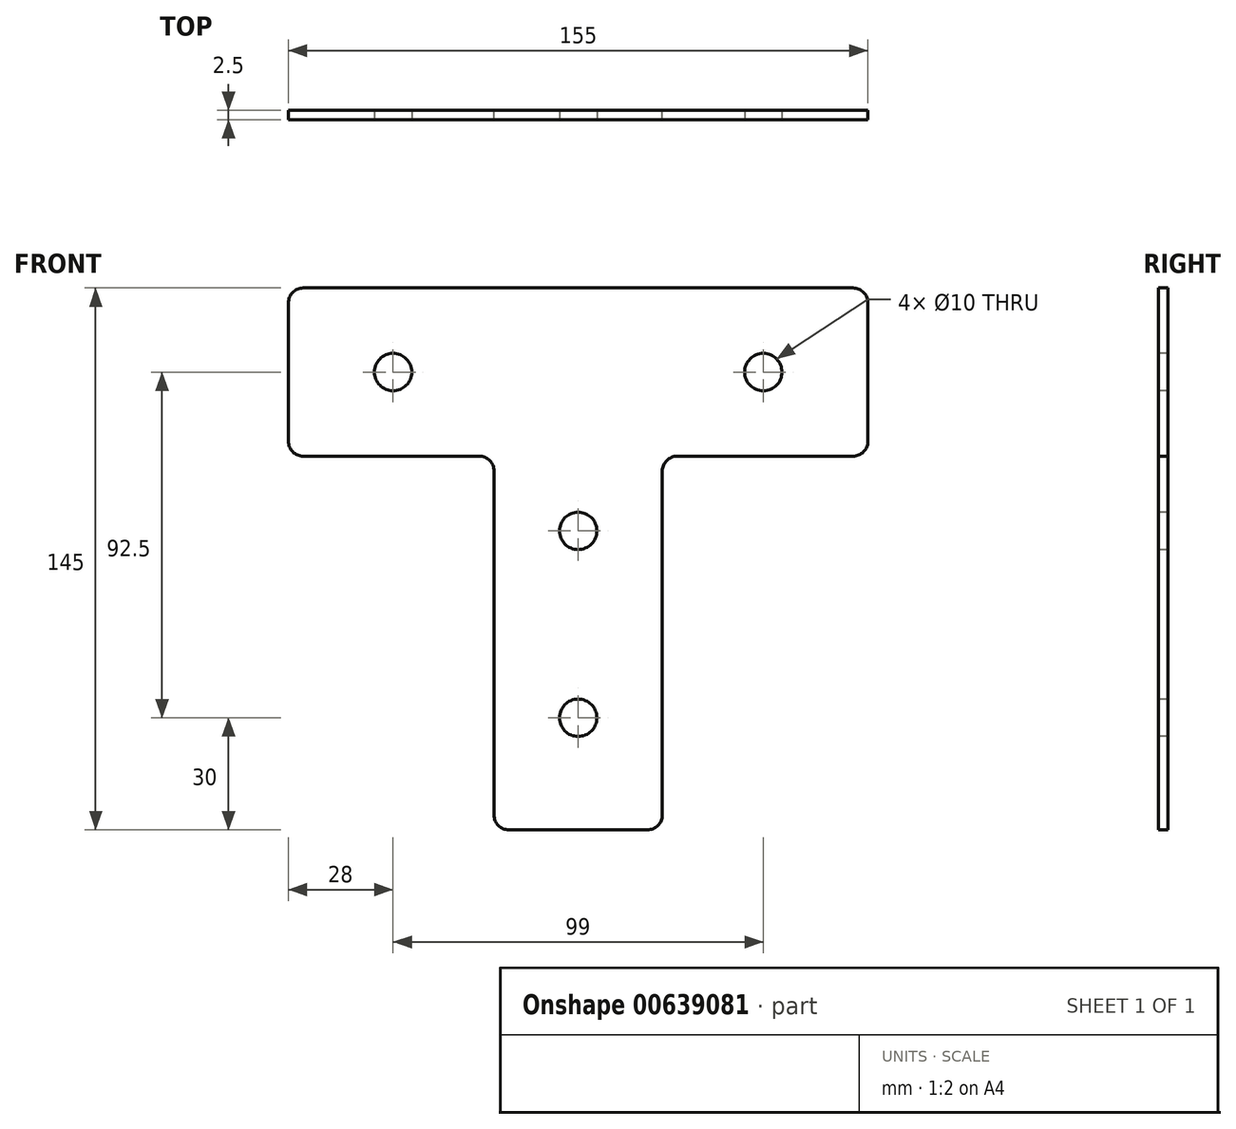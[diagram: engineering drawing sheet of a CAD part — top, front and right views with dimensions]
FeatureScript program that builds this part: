
annotation { "Feature Type Name" : "Feature", "Feature Type Description" : "" }
export const myFeature = defineFeature(function(context is Context, id is Id, definition is map)
    precondition{}
    {
        {
            var Q0;
            Q0=qCreatedBy(makeId("Front.planeOp"),FACE);
            var sketch = newSketch(context, id + "F0", { "sketchPlane" : qUnion([Q0])});
            skLineSegment(sketch, "E0.bottom", {"start": v(-77.5, 22.5) * mm, "end": v(77.5, 22.5) * mm});
            skLineSegment(sketch, "E0.top", {"start": v(-77.5, -22.5) * mm, "end": v(-22.5, -22.5) * mm});
            skLineSegment(sketch, "E0.left", {"start": v(-77.5, 22.5) * mm, "end": v(-77.5, -22.5) * mm});
            skLineSegment(sketch, "E0.right", {"start": v(77.5, 22.5) * mm, "end": v(77.5, -22.5) * mm});
            skPoint(sketch, "E0.middle", {"position": v(0, 0) * mm});
            skLineSegment(sketch, "E1", {"start": v(77.5, -22.5) * mm, "end": v(22.5, -22.5) * mm});
            skLineSegment(sketch, "E2", {"start": v(22.5, -22.5) * mm, "end": v(22.5, -122.5) * mm});
            skLineSegment(sketch, "E3", {"start": v(22.5, -122.5) * mm, "end": v(-22.5, -122.5) * mm});
            skLineSegment(sketch, "E4", {"start": v(-22.5, -122.5) * mm, "end": v(-22.5, -22.5) * mm});
            skLineSegment(sketch, "E5", {"start": v(-22.5, -22.5) * mm, "end": v(-77.5, -22.5) * mm});
            skLineSegment(sketch, "E6.trimOffspring", {"start": v(22.5, -22.5) * mm, "end": v(77.5, -22.5) * mm});
            skSolve(sketch);
        }
        {
            var Q0;
            Q0 = qSketchRegion(id + "F0", true);
            extrude(context, id + "F1", {"entities" : qUnion([Q0]), "depth" : 2.5 * mm, "offsetDistance" : 25 * mm});
        }
        {
            var Q0;
            Q0=makeQuery(id+"F1.opExtrude","SWEPT_EDGE",EDGE,{"disambiguationData":[OSD([sQuery(id+"F0.wireOp",EDGE,"E0.bottom"),sQuery(id+"F0.wireOp",EDGE,"E0.left")])]});
            var Q1;
            Q1=makeQuery(id+"F1.opExtrude","SWEPT_EDGE",EDGE,{"disambiguationData":[OSD([sQuery(id+"F0.wireOp",EDGE,"E0.left"),sQuery(id+"F0.wireOp",EDGE,"E5")])]});
            var Q2;
            Q2=makeQuery(id+"F1.opExtrude","SWEPT_EDGE",EDGE,{"disambiguationData":[OSD([sQuery(id+"F0.wireOp",EDGE,"E0.bottom"),sQuery(id+"F0.wireOp",EDGE,"E0.right")])]});
            var Q3;
            Q3=makeQuery(id+"F1.opExtrude","SWEPT_EDGE",EDGE,{"disambiguationData":[OSD([sQuery(id+"F0.wireOp",EDGE,"E0.right"),sQuery(id+"F0.wireOp",EDGE,"E6.trimOffspring")])]});
            var Q4;
            Q4=makeQuery(id+"F1.opExtrude","SWEPT_EDGE",EDGE,{"disambiguationData":[OSD([sQuery(id+"F0.wireOp",EDGE,"E2"),sQuery(id+"F0.wireOp",EDGE,"E3")])]});
            var Q5;
            Q5=makeQuery(id+"F1.opExtrude","SWEPT_EDGE",EDGE,{"disambiguationData":[OSD([sQuery(id+"F0.wireOp",EDGE,"E3"),sQuery(id+"F0.wireOp",EDGE,"E4")])]});
            var Q6;
            Q6=makeQuery(id+"F1.opExtrude","SWEPT_EDGE",EDGE,{"disambiguationData":[OSD([sQuery(id+"F0.wireOp",EDGE,"E2"),sQuery(id+"F0.wireOp",EDGE,"E6.trimOffspring")])]});
            var Q7;
            Q7=makeQuery(id+"F1.opExtrude","SWEPT_EDGE",EDGE,{"disambiguationData":[OSD([sQuery(id+"F0.wireOp",EDGE,"E4"),sQuery(id+"F0.wireOp",EDGE,"E5")])]});
            fillet(context, id + "F2", {"entities" : qUnion([Q0, Q1, Q2, Q3, Q4, Q5, Q6, Q7]), "radius" : 4 * mm, "tangentPropagation" : true, "allowEdgeOverflow" : false});
        }
        {
            var Q0;
            Q0=makeQuery(id+"F1.opExtrude","CAP_FACE",FACE,{"disambiguationData":[OSD([sQuery(id+"F0.wireOp",EDGE,"E0.bottom"),sQuery(id+"F0.wireOp",EDGE,"E0.left"),sQuery(id+"F0.wireOp",EDGE,"E0.right"),sQuery(id+"F0.wireOp",EDGE,"E2"),sQuery(id+"F0.wireOp",EDGE,"E3"),sQuery(id+"F0.wireOp",EDGE,"E4"),sQuery(id+"F0.wireOp",EDGE,"E5"),sQuery(id+"F0.wireOp",EDGE,"E6.trimOffspring")])],"isStart":false});
            var sketch = newSketch(context, id + "F3", { "sketchPlane" : qUnion([Q0])});
            skCircle(sketch, "E7", {"center": v(-49.5, 0) * mm, "radius": 5 * mm});
            skCircle(sketch, "E8", {"center": v(49.5, 0) * mm, "radius": 5 * mm});
            skCircle(sketch, "E9", {"center": v(0, -92.5) * mm, "radius": 5 * mm});
            skSolve(sketch);
        }
        {
            var Q0;
            Q0=makeQuery(id+"F3.imprint","IMPRINT",FACE,{"disambiguationData":[TD([[makeQuery(id+"F3.imprint","IMPRINT",EDGE,{"derivedFrom":sQuery(id+"F3.wireOp",EDGE,"E8")}),1.0]])]});
            var Q1;
            Q1=makeQuery(id+"F3.imprint","IMPRINT",FACE,{"disambiguationData":[TD([[makeQuery(id+"F3.imprint","IMPRINT",EDGE,{"derivedFrom":sQuery(id+"F3.wireOp",EDGE,"E7")}),1.0]])]});
            var Q2;
            Q2=makeQuery(id+"F3.imprint","IMPRINT",FACE,{"disambiguationData":[TD([[makeQuery(id+"F3.imprint","IMPRINT",EDGE,{"derivedFrom":sQuery(id+"F3.wireOp",EDGE,"E9")}),1.0]])]});
            extrude(context, id + "F4", {"entities" : qUnion([Q0, Q1, Q2]), "operationType" : NewBodyOperationType.REMOVE, "endBound" : BoundingType.THROUGH_ALL, "oppositeDirection" : true, "depth" : 25 * mm, "offsetDistance" : 25 * mm});
        }
        {
            var Q0;
            Q0=makeQuery(id+"F1.opExtrude","CAP_FACE",FACE,{"disambiguationData":[OSD([sQuery(id+"F0.wireOp",EDGE,"E0.bottom"),sQuery(id+"F0.wireOp",EDGE,"E0.left"),sQuery(id+"F0.wireOp",EDGE,"E0.right"),sQuery(id+"F0.wireOp",EDGE,"E2"),sQuery(id+"F0.wireOp",EDGE,"E3"),sQuery(id+"F0.wireOp",EDGE,"E4"),sQuery(id+"F0.wireOp",EDGE,"E5"),sQuery(id+"F0.wireOp",EDGE,"E6.trimOffspring")])],"isStart":false});
            var sketch = newSketch(context, id + "F5", { "sketchPlane" : qUnion([Q0])});
            skCircle(sketch, "E10", {"center": v(0, -42.5) * mm, "radius": 5 * mm});
            skSolve(sketch);
        }
        {
            var Q0;
            Q0=makeQuery(id+"F5.imprint","IMPRINT",FACE,{"disambiguationData":[TD([[makeQuery(id+"F5.imprint","IMPRINT",EDGE,{"derivedFrom":sQuery(id+"F5.wireOp",EDGE,"E10")}),1.0]])]});
            extrude(context, id + "F6", {"entities" : qUnion([Q0]), "operationType" : NewBodyOperationType.REMOVE, "endBound" : BoundingType.THROUGH_ALL, "oppositeDirection" : true, "depth" : 25 * mm, "offsetDistance" : 25 * mm});
        }
    });
